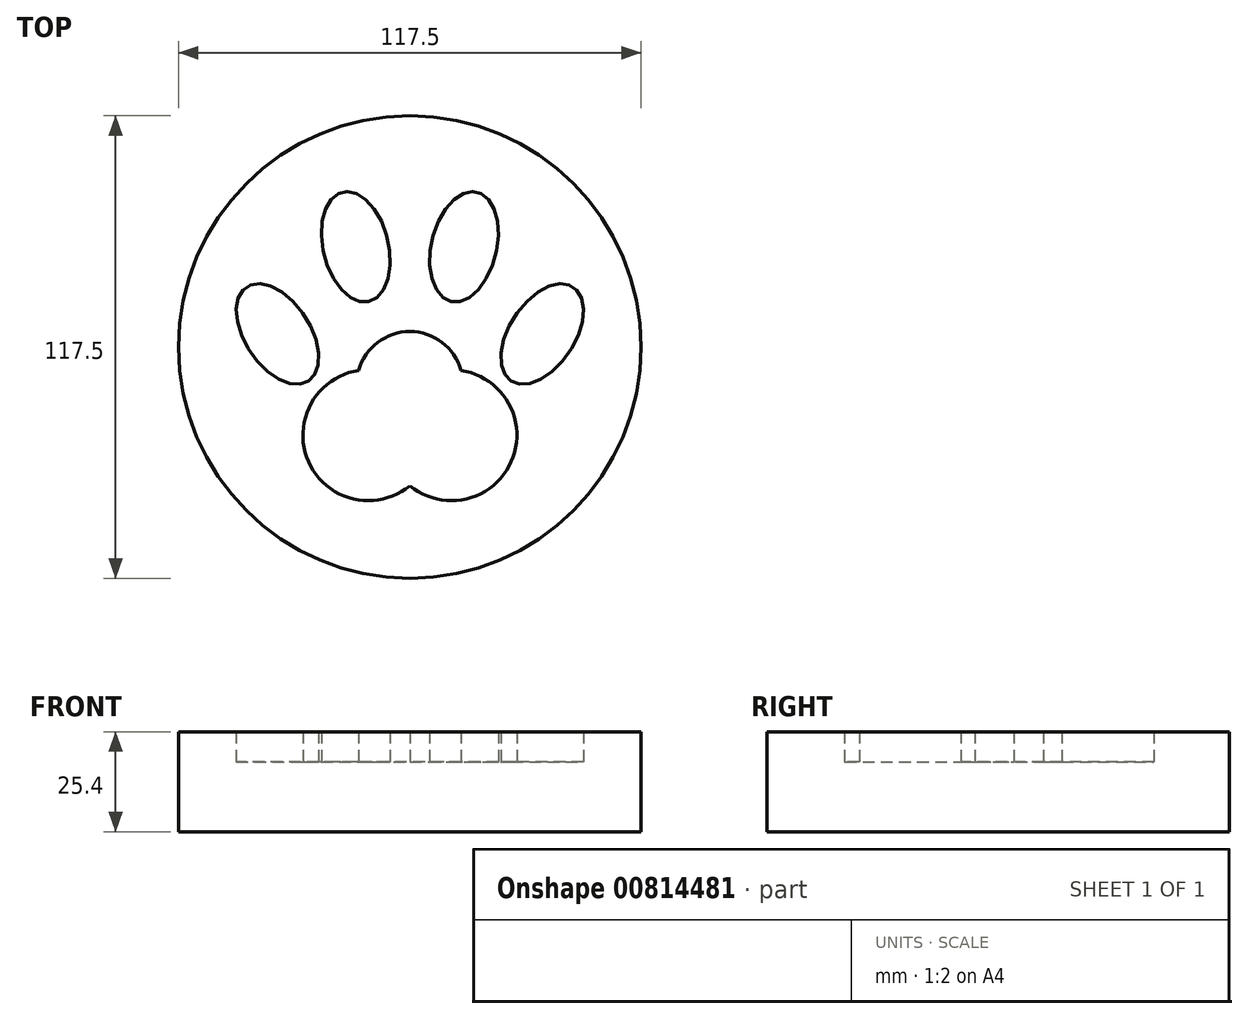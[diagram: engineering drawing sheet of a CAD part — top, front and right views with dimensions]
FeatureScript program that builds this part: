
annotation { "Feature Type Name" : "Feature", "Feature Type Description" : "" }
export const myFeature = defineFeature(function(context is Context, id is Id, definition is map)
    precondition{}
    {
        {
            var Q0;
            Q0=qCreatedBy(makeId("Top.planeOp"),FACE);
            var sketch = newSketch(context, id + "F0", { "sketchPlane" : qUnion([Q0])});
            skCircle(sketch, "E0", {"center": v(0, 0) * mm, "radius": 58.75 * mm});
            skSolve(sketch);
        }
        {
            var Q0;
            Q0=makeQuery(id+"F0.imprint","IMPRINT",FACE,{"disambiguationData":[TD([[makeQuery(id+"F0.imprint","IMPRINT",EDGE,{"derivedFrom":sQuery(id+"F0.wireOp",EDGE,"E0")}),1.0]])]});
            extrude(context, id + "F1", {"entities" : qUnion([Q0]), "depth" : 17.78 * mm, "offsetDistance" : 25.4 * mm});
        }
        {
            var Q0;
            Q0=makeQuery(id+"F1.opExtrude","CAP_FACE",FACE,{"disambiguationData":[OSD([sQuery(id+"F0.wireOp",EDGE,"E0")])],"isStart":false});
            var sketch = newSketch(context, id + "F2", { "sketchPlane" : qUnion([Q0])});
            skCircle(sketch, "E1", {"center": v(-10.55, -22.4) * mm, "radius": 16.63 * mm});
            skCircle(sketch, "E2.MirrorC", {"center": v(10.55, -22.4) * mm, "radius": 16.63 * mm});
            skEllipse(sketch, "E3", {"center": v(-13.75, 25.51) * mm, "majorRadius": 14.3 * mm, "minorRadius": 8.3 * mm, "majorAxis": v(0.23, -0.97)});
            skEllipse(sketch, "E4", {"center": v(-33.63, 3.31) * mm, "majorRadius": 14.3 * mm, "minorRadius": 8.3 * mm, "majorAxis": v(0.55, -0.83)});
            skEllipse(sketch, "E5.MirrorC", {"center": v(13.75, 25.51) * mm, "majorRadius": 14.3 * mm, "minorRadius": 8.3 * mm, "majorAxis": v(-0.23, -0.97)});
            skEllipse(sketch, "E6.MirrorC", {"center": v(33.63, 3.31) * mm, "majorRadius": 14.3 * mm, "minorRadius": 8.3 * mm, "majorAxis": v(-0.55, -0.83)});
            skCircle(sketch, "E7", {"center": v(0, -9.55) * mm, "radius": 13.48 * mm});
            skSolve(sketch);
        }
        {
            var Q0;
            Q0=makeQuery(id+"F2.imprint","IMPRINT",FACE,{"disambiguationData":[TD([[makeQuery(id+"F2.imprint","IMPRINT",EDGE,{"derivedFrom":sQuery(id+"F2.wireOp",EDGE,"E3")}),-1.0]])]});
            extrude(context, id + "F3", {"entities" : qUnion([Q0]), "operationType" : NewBodyOperationType.ADD, "depth" : 7.62 * mm, "offsetDistance" : 25.4 * mm});
        }
    });
